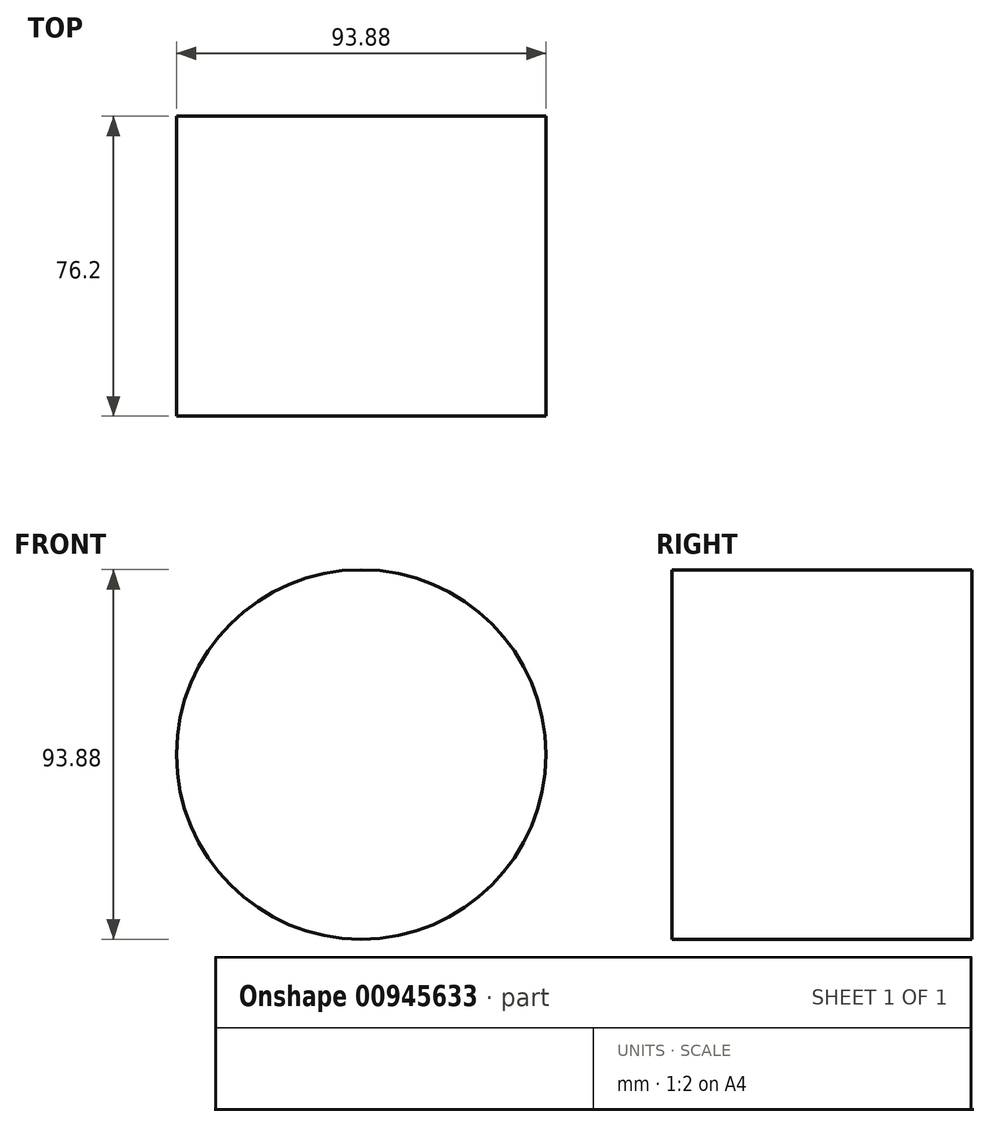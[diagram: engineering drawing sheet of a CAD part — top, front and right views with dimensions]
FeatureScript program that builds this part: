
annotation { "Feature Type Name" : "Feature", "Feature Type Description" : "" }
export const myFeature = defineFeature(function(context is Context, id is Id, definition is map)
    precondition{}
    {
        {
            var Q0;
            Q0=qCreatedBy(makeId("Front.planeOp"),FACE);
            var sketch = newSketch(context, id + "F0", { "sketchPlane" : qUnion([Q0])});
            skCircle(sketch, "E0", {"center": v(0, 0) * mm, "radius": 46.94 * mm});
            skSolve(sketch);
        }
        {
            var Q0;
            Q0 = qSketchRegion(id + "F0", true);
            extrude(context, id + "F1", {"entities" : qUnion([Q0]), "depth" : 76.2 * mm, "offsetDistance" : 25.4 * mm});
        }
    });
